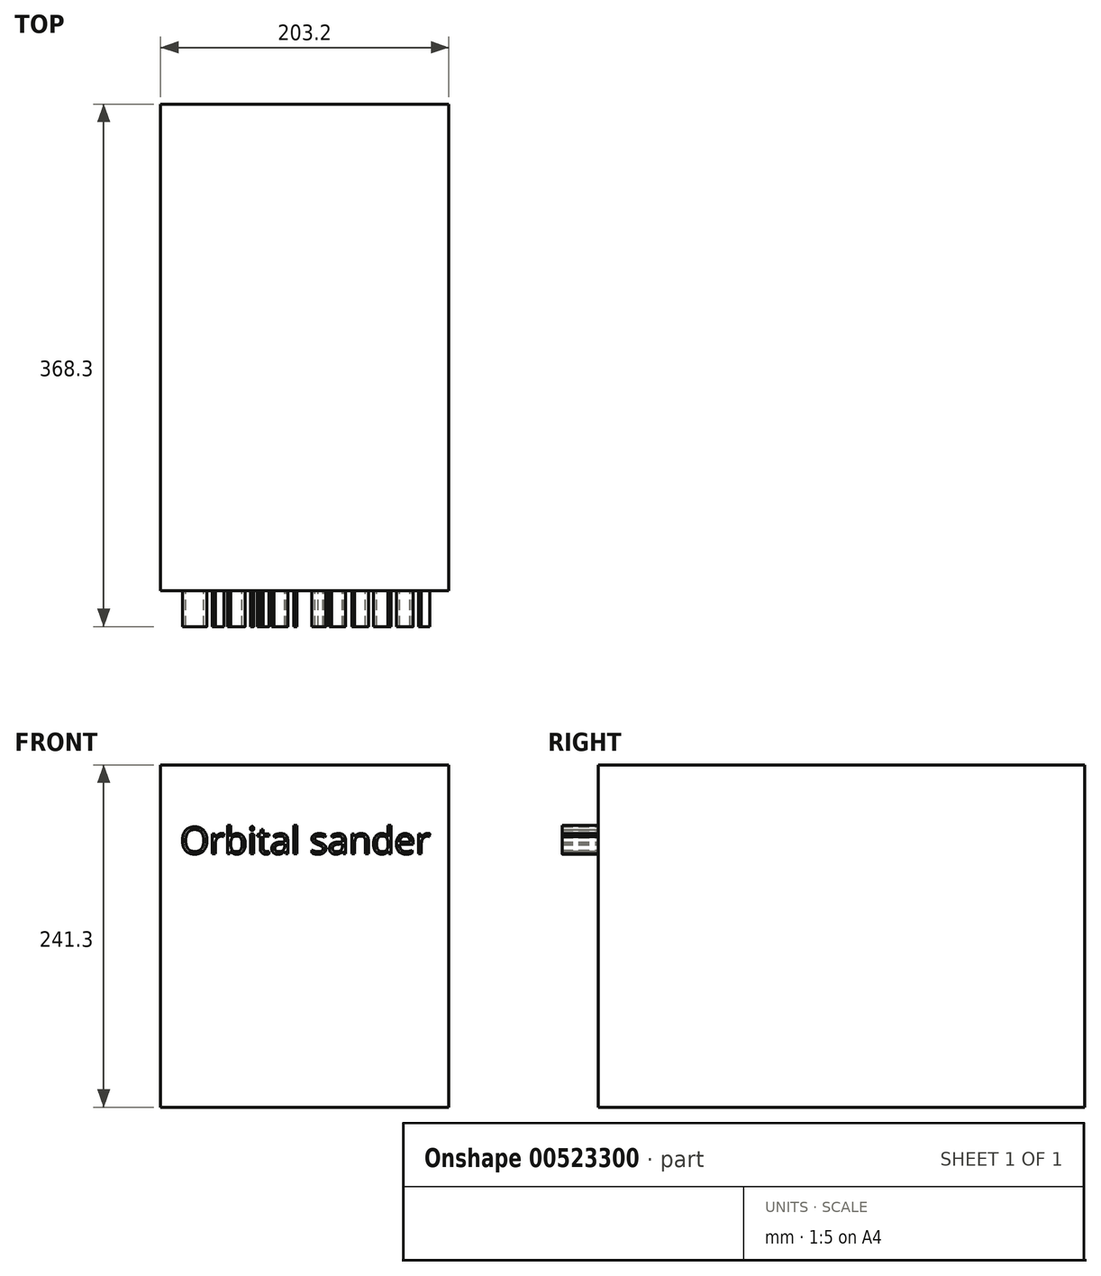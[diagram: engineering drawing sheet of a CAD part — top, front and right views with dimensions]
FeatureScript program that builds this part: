
annotation { "Feature Type Name" : "Feature", "Feature Type Description" : "" }
export const myFeature = defineFeature(function(context is Context, id is Id, definition is map)
    precondition{}
    {
        {
            var Q0;
            Q0=qCreatedBy(makeId("Front.planeOp"),FACE);
            var sketch = newSketch(context, id + "F0", { "sketchPlane" : qUnion([Q0])});
            skLineSegment(sketch, "E0.bottom", {"start": v(101.6, 120.65) * mm, "end": v(-101.6, 120.65) * mm});
            skLineSegment(sketch, "E0.top", {"start": v(101.6, -120.65) * mm, "end": v(-101.6, -120.65) * mm});
            skLineSegment(sketch, "E0.left", {"start": v(101.6, 120.65) * mm, "end": v(101.6, -120.65) * mm});
            skLineSegment(sketch, "E0.right", {"start": v(-101.6, 120.65) * mm, "end": v(-101.6, -120.65) * mm});
            skPoint(sketch, "E0.middle", {"position": v(0, 0) * mm});
            skSolve(sketch);
        }
        {
            var Q0;
            Q0=makeQuery(id+"F0.imprint","IMPRINT",FACE,{"disambiguationData":[TD([[makeQuery(id+"F0.imprint","IMPRINT",EDGE,{"derivedFrom":sQuery(id+"F0.wireOp",EDGE,"E0.bottom")}),1.0]])]});
            extrude(context, id + "F1", {"entities" : qUnion([Q0]), "depth" : 342.9 * mm, "offsetDistance" : 25.4 * mm});
        }
        {
            var Q0;
            Q0=makeQuery(id+"F1.opExtrude","CAP_FACE",FACE,{"disambiguationData":[OSD([sQuery(id+"F0.wireOp",EDGE,"E0.bottom"),sQuery(id+"F0.wireOp",EDGE,"E0.top"),sQuery(id+"F0.wireOp",EDGE,"E0.left"),sQuery(id+"F0.wireOp",EDGE,"E0.right")])],"isStart":false});
            var sketch = newSketch(context, id + "F2", { "sketchPlane" : qUnion([Q0])});
            skText(sketch, "E1", { "text": "Orbital sander", "fontName": "OpenSans-Regular.ttf"});
            const initialGuessF2  = {"E1": [-0.08778, 0.05791, 1, 0, 0.01895]};
            skSetInitialGuess(sketch, initialGuessF2);
            skSolve(sketch);
        }
        {
            var Q0;
            Q0 = qSketchRegion(id + "F2", true);
            extrude(context, id + "F3", {"entities" : qUnion([Q0]), "operationType" : NewBodyOperationType.ADD, "depth" : 25.4 * mm, "offsetDistance" : 25.4 * mm});
        }
    });
